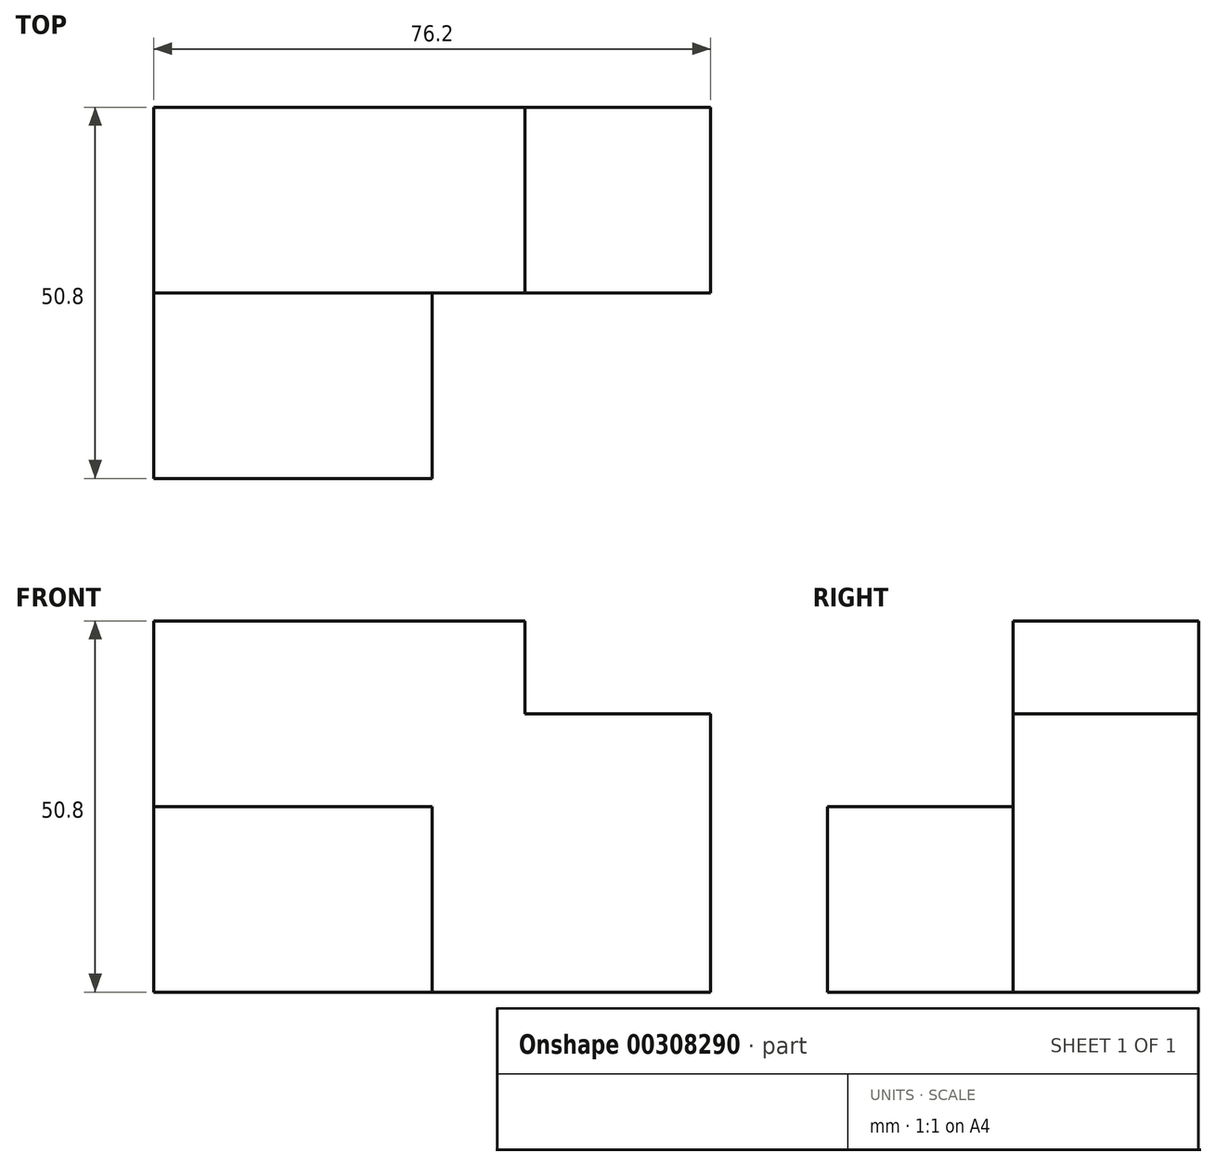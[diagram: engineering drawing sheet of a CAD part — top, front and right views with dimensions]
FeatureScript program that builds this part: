
annotation { "Feature Type Name" : "Feature", "Feature Type Description" : "" }
export const myFeature = defineFeature(function(context is Context, id is Id, definition is map)
    precondition{}
    {
        {
            var Q0;
            Q0=qCreatedBy(makeId("Front.planeOp"),FACE);
            var sketch = newSketch(context, id + "F0", { "sketchPlane" : qUnion([Q0])});
            skLineSegment(sketch, "E0", {"start": v(-32.06, 18.45) * mm, "end": v(-32.06, -32.35) * mm});
            skLineSegment(sketch, "E1", {"start": v(-32.06, -32.35) * mm, "end": v(44.14, -32.35) * mm});
            skLineSegment(sketch, "E2", {"start": v(44.14, -32.35) * mm, "end": v(44.14, 18.45) * mm});
            skLineSegment(sketch, "E3", {"start": v(44.14, 18.45) * mm, "end": v(-32.06, 18.45) * mm});
            skSolve(sketch);
        }
        {
            var Q0;
            Q0=makeQuery(id+"F0.imprint","IMPRINT",FACE,{"disambiguationData":[TD([[makeQuery(id+"F0.imprint","IMPRINT",EDGE,{"derivedFrom":sQuery(id+"F0.wireOp",EDGE,"E0")}),1.0]])]});
            extrude(context, id + "F1", {"entities" : qUnion([Q0]), "depth" : 25.4 * mm});
        }
        {
            var Q0;
            Q0=makeQuery(id+"F1.opExtrude","SWEPT_FACE",FACE,{"disambiguationData":[OSD([sQuery(id+"F0.wireOp",EDGE,"E3")])]});
            var sketch = newSketch(context, id + "F2", { "sketchPlane" : qUnion([Q0])});
            skLineSegment(sketch, "E4", {"start": v(18.74, 0) * mm, "end": v(18.74, -25.4) * mm});
            skLineSegment(sketch, "E5", {"start": v(18.74, 0) * mm, "end": v(44.14, 0) * mm});
            skSolve(sketch);
        }
        {
            var Q0;
            {var subQ0=sQuery(id+"F2.wireOp",EDGE,"E4");Q0=makeQuery(id+"F2.imprint","IMPRINT",FACE,{"disambiguationData":[TD([[makeQuery(id+"F2.imprint","IMPRINT",EDGE,{"derivedFrom":subQ0}),1.0]])]});}
            extrude(context, id + "F3", {"entities" : qUnion([Q0]), "operationType" : NewBodyOperationType.REMOVE, "oppositeDirection" : true, "depth" : 12.7 * mm});
        }
        {
            var Q0;
            Q0=makeQuery(id+"F1.opExtrude","CAP_FACE",FACE,{"disambiguationData":[OSD([sQuery(id+"F0.wireOp",EDGE,"E0"),sQuery(id+"F0.wireOp",EDGE,"E1"),sQuery(id+"F0.wireOp",EDGE,"E2"),sQuery(id+"F0.wireOp",EDGE,"E3")])],"isStart":false});
            var sketch = newSketch(context, id + "F4", { "sketchPlane" : qUnion([Q0])});
            skLineSegment(sketch, "E6", {"start": v(-32.06, -6.95) * mm, "end": v(6.04, -6.95) * mm});
            skLineSegment(sketch, "E7", {"start": v(6.04, -6.95) * mm, "end": v(6.04, -32.35) * mm});
            skSolve(sketch);
        }
        {
            var Q0;
            {var subQ0=sQuery(id+"F4.wireOp",EDGE,"E6");Q0=makeQuery(id+"F4.imprint","IMPRINT",FACE,{"disambiguationData":[TD([[makeQuery(id+"F4.imprint","IMPRINT",EDGE,{"derivedFrom":subQ0}),-1.0]])]});}
            extrude(context, id + "F5", {"entities" : qUnion([Q0]), "operationType" : NewBodyOperationType.ADD, "depth" : 25.4 * mm});
        }
    });
